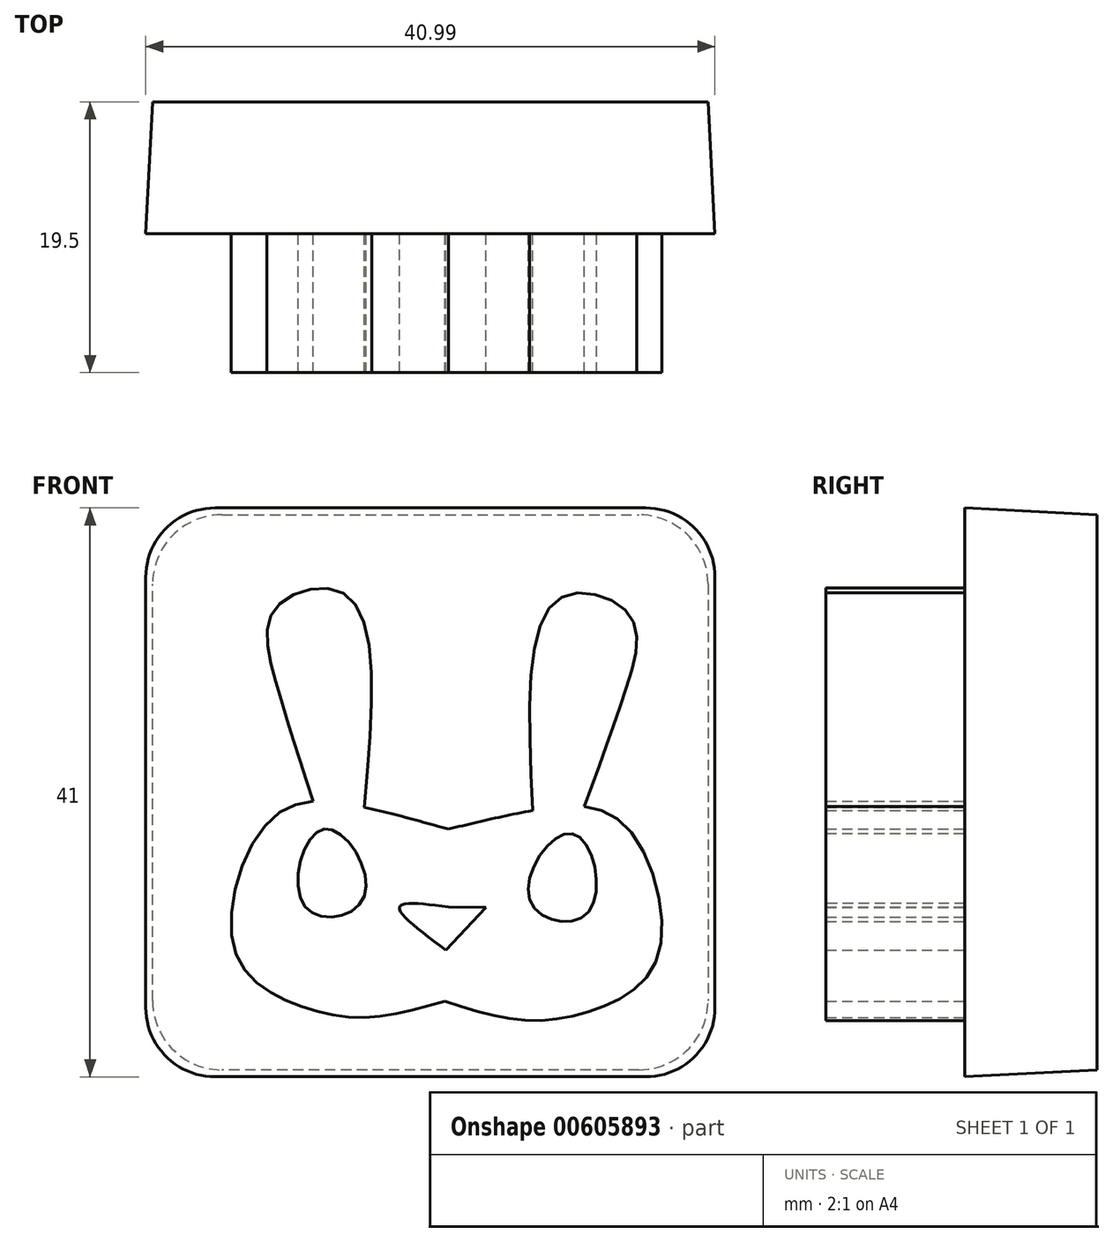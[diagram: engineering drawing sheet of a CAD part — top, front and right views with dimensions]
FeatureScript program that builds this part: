
annotation { "Feature Type Name" : "Feature", "Feature Type Description" : "" }
export const myFeature = defineFeature(function(context is Context, id is Id, definition is map)
    precondition{}
    {
        {
            var Q0;
            Q0=qCreatedBy(makeId("Front.planeOp"),FACE);
            var sketch = newSketch(context, id + "F0", { "sketchPlane" : qUnion([Q0])});
            skLineSegment(sketch, "E0.bottom", {"start": v(-5.85, 16.71) * mm, "end": v(34.15, 16.71) * mm});
            skLineSegment(sketch, "E0.top", {"start": v(-5.85, -23.29) * mm, "end": v(34.15, -23.29) * mm});
            skLineSegment(sketch, "E0.left", {"start": v(-5.85, 16.71) * mm, "end": v(-5.85, -23.29) * mm});
            skLineSegment(sketch, "E0.right", {"start": v(34.15, 16.71) * mm, "end": v(34.15, -23.29) * mm});
            skSolve(sketch);
        }
        {
            var Q0;
            Q0=makeQuery(id+"F0.imprint","IMPRINT",FACE,{"disambiguationData":[TD([[makeQuery(id+"F0.imprint","IMPRINT",EDGE,{"derivedFrom":sQuery(id+"F0.wireOp",EDGE,"E0.bottom")}),-1.0]])]});
            extrude(context, id + "F1", {"entities" : qUnion([Q0]), "depth" : 9.5 * mm, "offsetDistance" : 25 * mm, "hasDraft" : true, "draftAngle" : 3 * degree});
        }
        {
            var Q0;
            Q0=makeQuery(id+"F1.opExtrude","CAP_FACE",FACE,{"disambiguationData":[OSD([sQuery(id+"F0.wireOp",EDGE,"E0.bottom"),sQuery(id+"F0.wireOp",EDGE,"E0.top"),sQuery(id+"F0.wireOp",EDGE,"E0.left"),sQuery(id+"F0.wireOp",EDGE,"E0.right")])],"isStart":false});
            var sketch = newSketch(context, id + "F2", { "sketchPlane" : qUnion([Q0])});
            skFitSpline(sketch, "E1", {"points": [v(15.44, -5.94) * mm, v(9.4, -4.36) * mm, v(3, -4.95) * mm, v(0, -14.45) * mm, v(4.36, -18.52) * mm, v(9.6, -19.5) * mm, v(15.21, -18.34) * mm], "startDerivative": vector(-35.84, 10.1) * mm, "endDerivative": vector(36.32, 10.37) * mm});
            skFitSpline(sketch, "E2", {"points": [v(5.7, -3.94) * mm, v(3, 4.75) * mm, v(3, 9.99) * mm, v(8.05, 10.96) * mm, v(9.4, -4.36) * mm], "startDerivative": vector(-11.04, 34.2) * mm, "endDerivative": vector(-5.26, -59.75) * mm});
            skFitSpline(sketch, "E3", {"points": [v(6.5, -5.94) * mm, v(5.14, -11.54) * mm, v(9.4, -10.77) * mm, v(6.5, -5.94) * mm]});
            skFitSpline(sketch, "E4", {"points": [v(15.44, -11.54) * mm, v(11.93, -11.54) * mm, v(15.28, -14.66) * mm], "startDerivative": vector(-10.75, 1.37) * mm, "endDerivative": vector(9.97, -7.41) * mm});
            skFitSpline(sketch, "E5.MirrorCS", {"points": [v(25.25, -4.3) * mm, v(28.27, 4.28) * mm, v(28.46, 9.51) * mm, v(23.46, 10.67) * mm, v(21.53, -4.6) * mm], "startDerivative": vector(12.3, 33.76) * mm, "endDerivative": vector(3.03, -59.9) * mm});
            skFitSpline(sketch, "E6.MirrorCS", {"points": [v(15.44, -5.94) * mm, v(21.53, -4.6) * mm, v(27.9, -5.41) * mm, v(30.56, -15.02) * mm, v(26.04, -18.93) * mm, v(20.78, -19.7) * mm, v(15.21, -18.34) * mm], "startDerivative": vector(36.2, 8.75) * mm, "endDerivative": vector(-35.9, 11.72) * mm});
            skFitSpline(sketch, "E7.MirrorC", {"points": [v(24.38, -6.27) * mm, v(25.53, -11.92) * mm, v(21.3, -10.99) * mm, v(24.38, -6.27) * mm]});
            skLineSegment(sketch, "E8", {"start": v(15.44, -11.54) * mm, "end": v(18.15, -11.6) * mm});
            skLineSegment(sketch, "E9", {"start": v(18.15, -11.6) * mm, "end": v(15.28, -14.66) * mm});
            skSolve(sketch);
        }
        {
            var Q0;
            Q0=qSketchRegion(id+"F2",true);
            extrude(context, id + "F3", {"entities" : qUnion([Q0]), "operationType" : NewBodyOperationType.ADD, "depth" : 10 * mm, "offsetDistance" : 25 * mm});
        }
        {
            var Q0;
            Q0=makeQuery(id+"F1.opExtrude","SWEPT_EDGE",EDGE,{"disambiguationData":[OSD([sQuery(id+"F0.wireOp",EDGE,"E0.bottom"),sQuery(id+"F0.wireOp",EDGE,"E0.left")])]});
            var Q1;
            Q1=makeQuery(id+"F1.opExtrude","SWEPT_EDGE",EDGE,{"disambiguationData":[OSD([sQuery(id+"F0.wireOp",EDGE,"E0.bottom"),sQuery(id+"F0.wireOp",EDGE,"E0.right")])]});
            var Q2;
            Q2=makeQuery(id+"F1.opExtrude","SWEPT_EDGE",EDGE,{"disambiguationData":[OSD([sQuery(id+"F0.wireOp",EDGE,"E0.top"),sQuery(id+"F0.wireOp",EDGE,"E0.right")])]});
            var Q3;
            Q3=makeQuery(id+"F1.opExtrude","SWEPT_EDGE",EDGE,{"disambiguationData":[OSD([sQuery(id+"F0.wireOp",EDGE,"E0.top"),sQuery(id+"F0.wireOp",EDGE,"E0.left")])]});
            fillet(context, id + "F4", {"entities" : qUnion([Q0, Q1, Q2, Q3]), "radius" : 5 * mm, "tangentPropagation" : true, "allowEdgeOverflow" : false});
        }
    });
